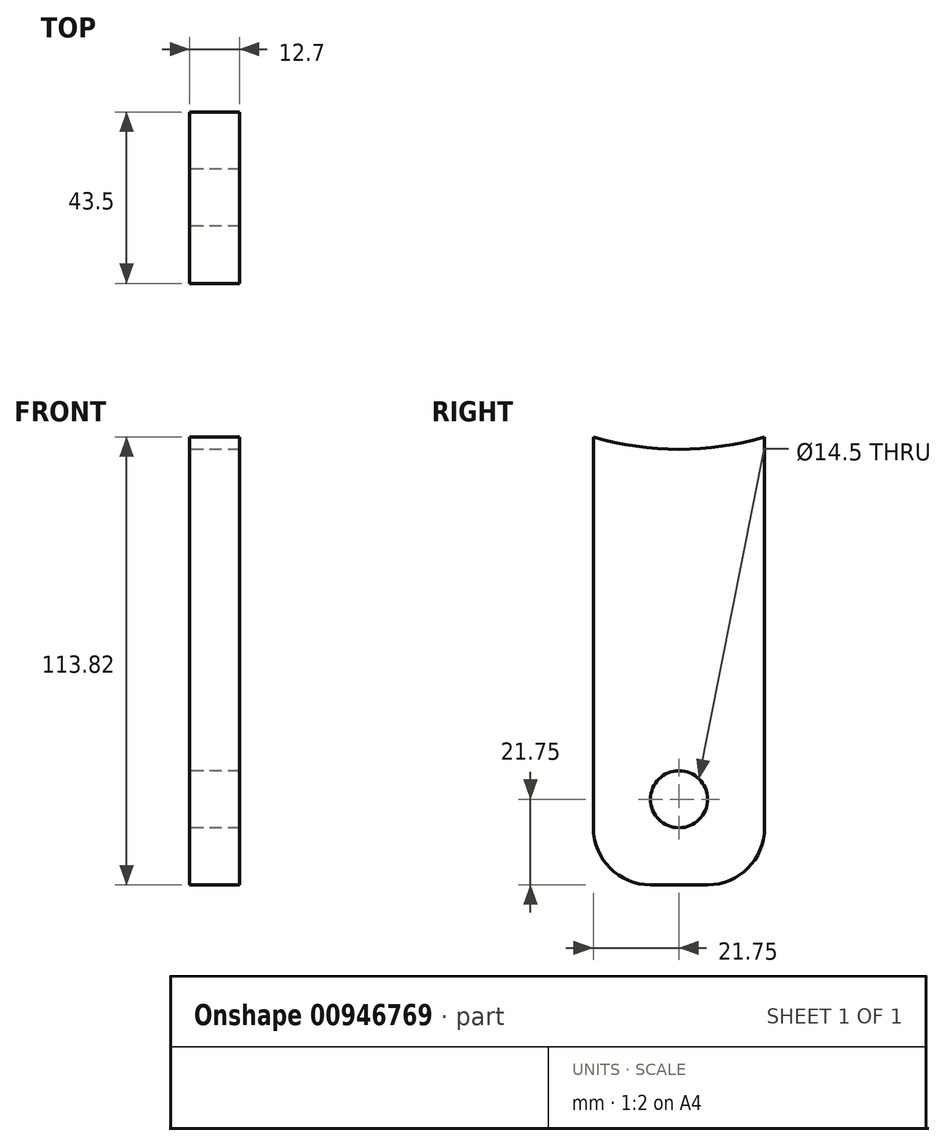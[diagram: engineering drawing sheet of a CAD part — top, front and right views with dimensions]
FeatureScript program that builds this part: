
annotation { "Feature Type Name" : "Feature", "Feature Type Description" : "" }
export const myFeature = defineFeature(function(context is Context, id is Id, definition is map)
    precondition{}
    {
        {
            var Q0;
            Q0=qCreatedBy(makeId("Right.planeOp"),FACE);
            var sketch = newSketch(context, id + "F0", { "sketchPlane" : qUnion([Q0])});
            skCircle(sketch, "E0", {"center": v(0, 0) * mm, "radius": 7.25 * mm});
            skLineSegment(sketch, "E1.bottom", {"start": v(-7.25, -21.75) * mm, "end": v(7.25, -21.75) * mm});
            skLineSegment(sketch, "E1.left", {"start": v(-21.75, -7.25) * mm, "end": v(-21.75, 92.07) * mm});
            skLineSegment(sketch, "E1.right", {"start": v(21.75, -7.25) * mm, "end": v(21.75, 92.07) * mm});
            skPoint(sketch, "E2.visualSharp", {"position": v(-21.75, -21.75) * mm});
            skArc(sketch, "E2.filletArc", {"start": v(-21.75, -7.25) * mm, "mid": v(-17.5, -17.5) * mm, "end": v(-7.25, -21.75) * mm});
            skPoint(sketch, "E3.visualSharp", {"position": v(21.75, -21.75) * mm});
            skArc(sketch, "E3.filletArc", {"start": v(7.25, -21.75) * mm, "mid": v(17.5, -17.5) * mm, "end": v(21.75, -7.25) * mm});
            skCircle(sketch, "E4", {"center": v(0, 165.1) * mm, "radius": 9.66 * mm, "construction": true});
            skArc(sketch, "E5", {"start": v(-21.75, 92.07) * mm, "mid": v(0, 88.9) * mm, "end": v(21.75, 92.07) * mm});
            skSolve(sketch);
        }
        {
            var Q0;
            Q0=makeQuery(id+"F0.imprint","IMPRINT",FACE,{"disambiguationData":[TD([[makeQuery(id+"F0.imprint","IMPRINT",EDGE,{"derivedFrom":sQuery(id+"F0.wireOp",EDGE,"E0")}),-1.0]])]});
            extrude(context, id + "F1", {"entities" : qUnion([Q0]), "depth" : 12.7 * mm, "offsetDistance" : 25.4 * mm});
        }
    });
